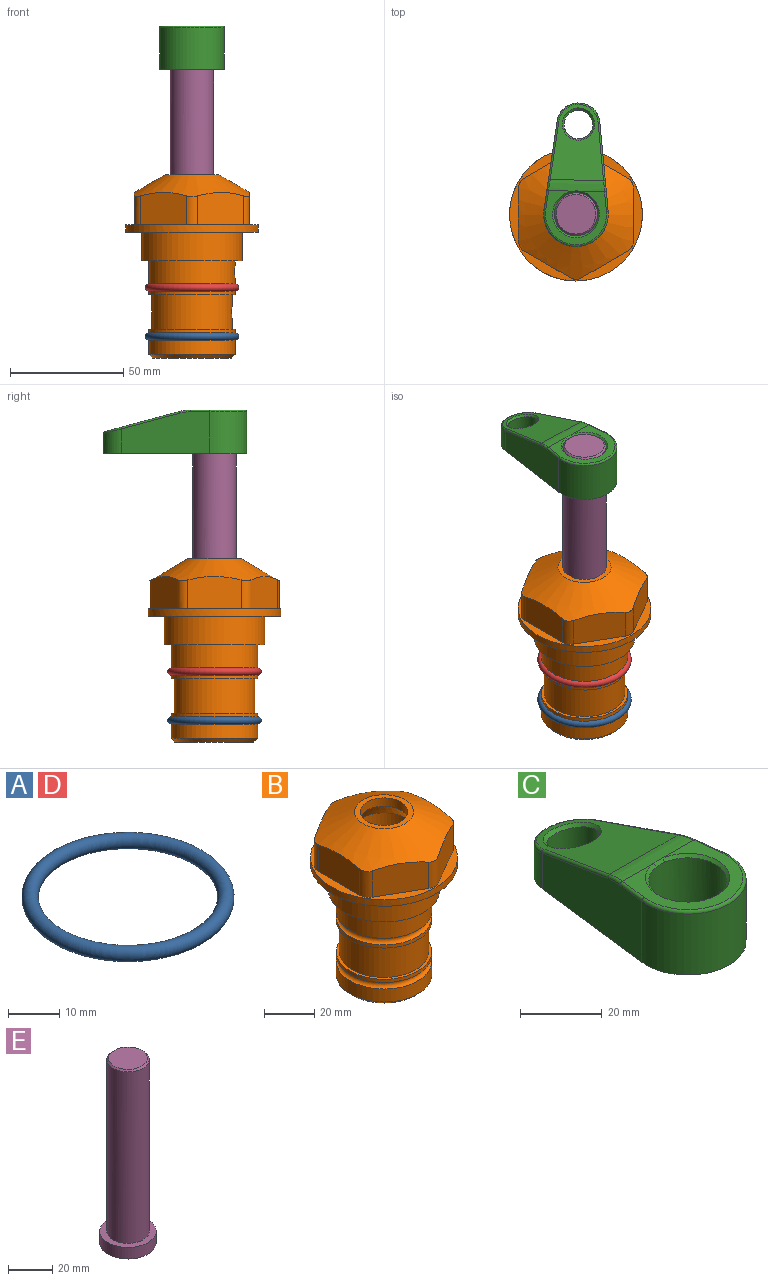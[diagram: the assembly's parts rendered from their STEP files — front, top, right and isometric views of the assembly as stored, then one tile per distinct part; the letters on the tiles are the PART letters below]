
ASSEMBLY  parts=5 mates=4
PART A: 1 faces, bbox 44.7x44.7x3.2 mm
  f0: torus R=19.05mm, axis (0,0,1), area 1193.9mm2
PART B: 36 faces, bbox 58.7x58.7x81 mm
  f0: cylinder r=17.78mm len=35.56mm, axis (0,0,1), area 1670.8mm2, adj f23,f24,f31
  f1: cylinder r=19.05mm len=38.1mm, axis (0,0,1), area 1191.9mm2, adj f26,f27,f30
  f2: plane 58.66x58.66mm, normal (0,0,-1), area 1150.6mm2, adj f3,f28
  f3: cylinder r=29.33mm len=58.66mm, axis (0,0,-1), area 585.1mm2, adj f2,f4
  f4: plane 58.66x58.66mm, normal (0,0,1), area 475.9mm2, adj f3,f5,f6,f7,f8,f9,f10,f11
  f5: plane 20.32x14.34mm, normal (-0.5,0.87,0), area 324.4mm2, adj f4,f15,f16,f17
  f6: plane 20.32x14.34mm, normal (0.5,0.87,0), area 324.4mm2, adj f4,f14,f15,f17
  f7: plane 23.48x14.34mm, normal (1,0,0), area 324.4mm2, adj f4,f13,f14,f17
  f8: plane 20.32x14.34mm, normal (0.5,-0.87,0), area 324.4mm2, adj f4,f12,f13,f17
  f9: plane 20.32x14.34mm, normal (-0.5,-0.87,0), area 324.4mm2, adj f4,f11,f12,f17
  f10: plane 23.48x14.34mm, normal (-1,0,0), area 324.4mm2, adj f4,f11,f16,f17
  f11: cylinder r=5.08mm len=12.85mm, axis (0,0,-1), area 67.2mm2, adj f4,f9,f10,f17
  f12: cylinder r=5.08mm len=12.85mm, axis (0,0,-1), area 67.2mm2, adj f4,f8,f9,f17
  f13: cylinder r=5.08mm len=12.85mm, axis (0,0,-1), area 67.2mm2, adj f4,f7,f8,f17
  f14: cylinder r=5.08mm len=12.85mm, axis (0,0,-1), area 67.2mm2, adj f4,f6,f7,f17
  f15: cylinder r=5.08mm len=12.85mm, axis (0,0,-1), area 67.2mm2, adj f4,f5,f6,f17
  f16: cylinder r=5.08mm len=12.85mm, axis (0,0,-1), area 67.2mm2, adj f4,f5,f10,f17
  f17: cone r=11.73mm half-angle=60deg, axis (0,0,-1), area 2071.8mm2, adj f5,f6,f7,f8,f9,f10,f11,f12
  f18: plane 23.46x23.46mm, normal (0,0,1), area 147.4mm2, adj f17,f35
  f19: plane 34.93x34.93mm, normal (0,0,-1), area 958mm2, adj f29
  f20: cylinder r=19.05mm len=38.1mm, axis (0,0,1), area 760.1mm2, adj f21,f29
  f21: torus R=19.05mm, axis (0,0,1), area 565.3mm2, adj f20,f22
  f22: cylinder r=19.05mm len=38.1mm, axis (0,0,1), area 190mm2, adj f21,f23
  f23: plane 38.1x38.1mm, normal (0,0,1), area 146.9mm2, adj f0,f22
  f24: plane 38.1x38.1mm, normal (0,0,-1), area 146.9mm2, adj f0,f25
  f25: cylinder r=19.05mm len=38.1mm, axis (0,0,1), area 190mm2, adj f24,f26
  f26: torus R=19.05mm, axis (0,0,1), area 565.3mm2, adj f1,f25
  f27: plane 44.45x44.45mm, normal (0,0,-1), area 411.7mm2, adj f1,f28
  f28: cylinder r=22.23mm len=44.45mm, axis (0,0,1), area 1773.5mm2, adj f2,f27
  f29: cone r=19.05mm half-angle=45deg, axis (0,0,1), area 257.5mm2, adj f19,f20
  f30: cylinder r=3.17mm len=6.75mm, axis (-1,0,0), area 128mm2, adj f1,f33
  f31: cylinder r=3.17mm len=6.35mm, axis (-1,0,0), area 102.5mm2, adj f0,f33
  f32: plane 25.4x25.4mm, normal (0,0,1), area 506.7mm2, adj f33
  f33: cylinder r=12.7mm len=66.42mm, axis (0,0,-1), area 5236.2mm2, adj f30,f31,f32,f34
  f34: cone r=9.53mm half-angle=30deg, axis (0,0,-1), area 443.4mm2, adj f33,f35
  f35: cylinder r=9.53mm len=19.05mm, axis (0,0,-1), area 240.9mm2, adj f18,f34
PART C: 31 faces, bbox 31.7x65.5x19.8 mm
  f0: plane 39.12x18.26mm, normal (0.99,0.12,0), area 612.2mm2, adj f1,f4,f7,f11,f13,f15
  f1: cylinder r=9.53mm len=18.91mm, axis (0,0,-1), area 296.1mm2, adj f0,f2,f7,f17
  f2: plane 39.12x18.26mm, normal (-0.99,0.12,0), area 612.2mm2, adj f1,f4,f7,f12,f14,f16
  f3: cylinder r=6.35mm len=12.7mm, axis (0,0,-1), area 362.4mm2, adj f7,f18
  f4: cylinder r=14.29mm len=28.58mm, axis (0,0,-1), area 882.2mm2, adj f0,f2,f7,f10
  f5: cylinder r=9.53mm len=19.05mm, axis (0,0,-1), area 1092.6mm2, adj f7,f19,f20
  f6: plane 26.99x23.69mm, normal (0,0,1), area 216.2mm2, adj f9,f10,f11,f12,f19
  f7: plane 63.5x28.58mm, normal (0,0,-1), area 661.8mm2, adj f0,f1,f2,f3,f4,f5,f22,f23
  f8: plane 33.52x23.6mm, normal (0,0.26,0.97), area 486mm2, adj f9,f15,f16,f17,f18
  f9: cylinder r=19.05mm len=24.72mm, axis (1,0,0), area 120.4mm2, adj f6,f8,f13,f14,f20
  f10: torus R=13.49mm, axis (0,0,1), area 59mm2, adj f4,f6,f11,f12
  f11: cylinder r=0.79mm len=8.67mm, axis (0.12,-0.99,0), area 10.8mm2, adj f0,f6,f10,f13
  f12: cylinder r=0.79mm len=8.67mm, axis (0.12,0.99,0), area 10.8mm2, adj f2,f6,f10,f14
  f13: bspline ~4.95x1.42mm, area 6.1mm2, adj f0,f9,f11,f15
  f14: bspline ~4.95x1.42mm, area 6.1mm2, adj f2,f9,f12,f16
  f15: cylinder r=0.79mm len=25.95mm, axis (0.12,-0.96,0.26), area 32.9mm2, adj f0,f8,f13,f17
  f16: cylinder r=0.79mm len=25.95mm, axis (0.12,0.96,-0.26), area 32.9mm2, adj f2,f8,f14,f17
  f17: bspline ~18.91x8.38mm, area 30mm2, adj f1,f8,f15,f16
  f18: bspline ~14.29x14.29mm, area 48.3mm2, adj f3,f8
  f19: cone r=9.53mm half-angle=45deg, axis (0,0,1), area 66.5mm2, adj f5,f6,f20
  f20: bspline ~3.22x0.96mm, area 3.5mm2, adj f5,f9,f19
  f21: plane 2.75x2.72mm, normal (0,0,-1), area 2.9mm2, adj f23,f25,f28
  f22: plane 23.05x15.88mm, normal (-0.99,-0.12,0), area 323.6mm2, adj f7,f25,f26,f27,f28,f29
  f23: plane 23.05x15.88mm, normal (0.99,-0.12,0), area 323.6mm2, adj f7,f21,f25,f27,f28,f30
  f24: cylinder r=9.53mm len=10.69mm, axis (0,0,-1), area 114.7mm2, adj f7,f27,f29,f30
  f25: cylinder r=12.7mm len=20.59mm, axis (0,0,-1), area 381.1mm2, adj f7,f21,f22,f23,f26,f28
  f26: plane 2.75x2.72mm, normal (0,0,-1), area 2.9mm2, adj f22,f25,f28
  f27: plane 19.72x18.37mm, normal (0,-0.26,-0.97), area 291.8mm2, adj f22,f23,f24,f28,f29,f30
  f28: cylinder r=15.88mm len=19.92mm, axis (1,0,0), area 54.8mm2, adj f21,f22,f23,f25,f26,f27
  f29: cylinder r=1.59mm len=11mm, axis (0,0,-1), area 34.7mm2, adj f7,f22,f24,f27
  f30: cylinder r=1.59mm len=11mm, axis (0,0,-1), area 34.7mm2, adj f7,f23,f24,f27
PART D: same geometry as A
PART E: 6 faces, bbox 25.4x25.4x101.6 mm
  f0: plane 17.46x17.46mm, normal (0,0,1), area 239.5mm2, adj f5
  f1: plane 25.4x25.4mm, normal (0,0,-1), area 506.7mm2, adj f2
  f2: cylinder r=12.7mm len=25.4mm, axis (0,0,1), area 506.7mm2, adj f1,f3
  f3: plane 25.4x25.4mm, normal (0,0,1), area 221.7mm2, adj f2,f4
  f4: cylinder r=9.53mm len=94.46mm, axis (0,0,1), area 5653mm2, adj f3,f5
  f5: cone r=8.73mm half-angle=45deg, axis (0,0,-1), area 64.4mm2, adj f0,f4
PLACE A t=(0,0,-21.59)mm
PLACE B at identity fixed
PLACE C rot(axis=(0,0,-1),1.5deg) t=(0,0,27.55)mm
PLACE D at identity
PLACE E rot(axis=(0,0,-1),1.5deg) t=(0,0,27.55)mm
MATE cylindrical E.f2 <-> B.f0  axis (0,0,-1) through (0,0,-10.55)mm
MATE fastened E.f2 <-> C.f4  axis (0,0,1) through (0,0,91.05)mm
MATE fastened A.f0 <-> B.f0  axis (0,0,1) through (0,0,-46.1)mm
MATE fastened D.f0 <-> B.f0  axis (0,0,1) through (0,0,-24.51)mm
